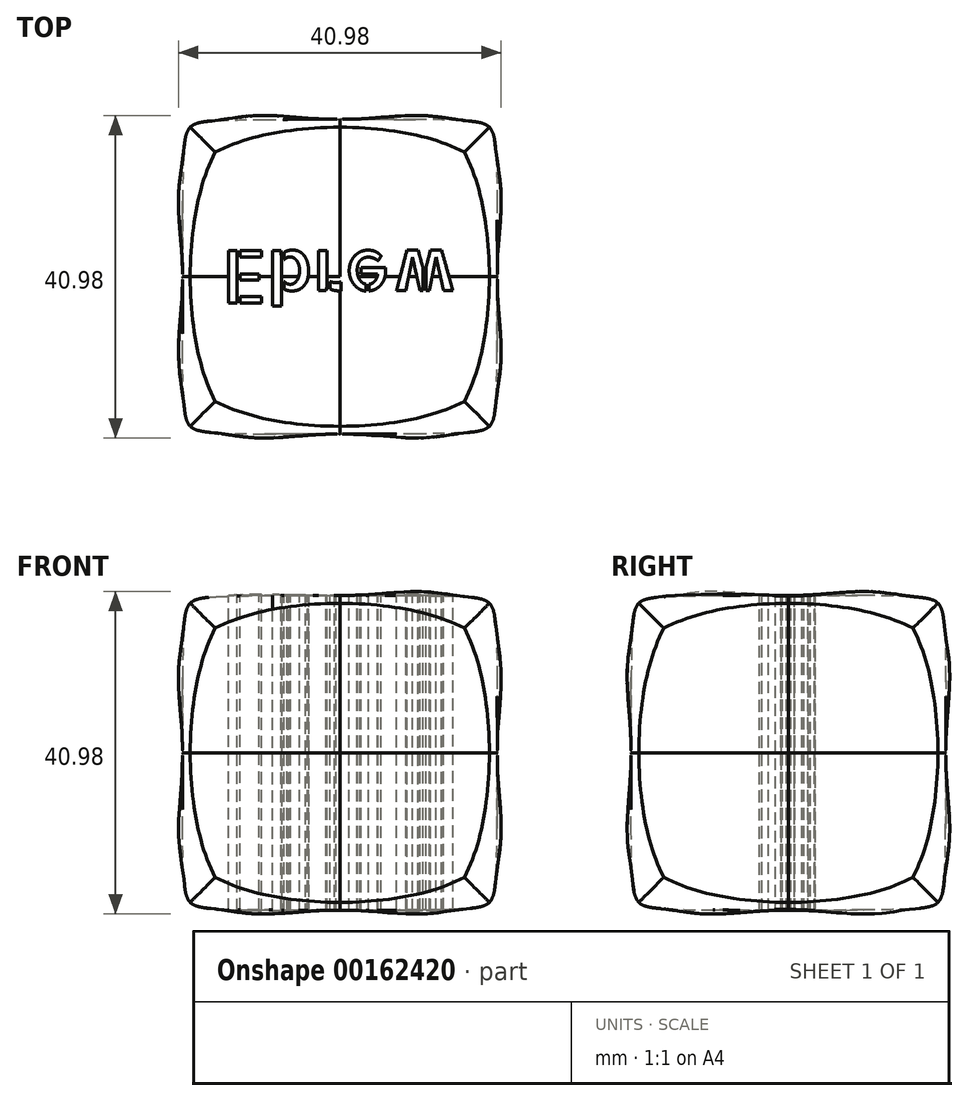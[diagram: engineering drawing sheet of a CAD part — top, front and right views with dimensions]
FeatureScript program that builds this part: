
annotation { "Feature Type Name" : "Feature", "Feature Type Description" : "" }
export const myFeature = defineFeature(function(context is Context, id is Id, definition is map)
    precondition{}
    {
        {
            var Q0;
            Q0=qCreatedBy(makeId("Top.planeOp"),FACE);
            var sketch = newSketch(context, id + "F0", { "sketchPlane" : qUnion([Q0])});
            skLineSegment(sketch, "E0.bottom", {"start": v(20, -20) * mm, "end": v(-20, -20) * mm});
            skLineSegment(sketch, "E0.top", {"start": v(20, 20) * mm, "end": v(-20, 20) * mm});
            skLineSegment(sketch, "E0.left", {"start": v(20, -20) * mm, "end": v(20, 20) * mm});
            skLineSegment(sketch, "E0.right", {"start": v(-20, -20) * mm, "end": v(-20, 20) * mm});
            skPoint(sketch, "E0.middle", {"position": v(0, 0) * mm});
            skSolve(sketch);
        }
        {
            var Q0;
            Q0 = qSketchRegion(id + "F0", true);
            extrude(context, id + "F1", {"entities" : qUnion([Q0]), "depth" : 40 * mm});
        }
        {
            var Q0;
            Q0=makeQuery(id+"F1.opExtrude","CAP_EDGE",EDGE,{"disambiguationData":[OSD([sQuery(id+"F0.wireOp",EDGE,"E0.right")])],"isStart":false});
            var Q1;
            Q1=makeQuery(id+"F1.opExtrude","SWEPT_FACE",FACE,{"disambiguationData":[OSD([sQuery(id+"F0.wireOp",EDGE,"E0.bottom")])]});
            var Q2;
            Q2=makeQuery(id+"F1.opExtrude","CAP_FACE",FACE,{"disambiguationData":[OSD([sQuery(id+"F0.wireOp",EDGE,"E0.bottom"),sQuery(id+"F0.wireOp",EDGE,"E0.top"),sQuery(id+"F0.wireOp",EDGE,"E0.left"),sQuery(id+"F0.wireOp",EDGE,"E0.right")])],"isStart":false});
            var Q3;
            Q3=makeQuery(id+"F1.opExtrude","SWEPT_FACE",FACE,{"disambiguationData":[OSD([sQuery(id+"F0.wireOp",EDGE,"E0.right")])]});
            var Q4;
            Q4=makeQuery(id+"F1.opExtrude","CAP_FACE",FACE,{"disambiguationData":[OSD([sQuery(id+"F0.wireOp",EDGE,"E0.bottom"),sQuery(id+"F0.wireOp",EDGE,"E0.top"),sQuery(id+"F0.wireOp",EDGE,"E0.left"),sQuery(id+"F0.wireOp",EDGE,"E0.right")])],"isStart":true});
            var Q5;
            Q5=makeQuery(id+"F1.opExtrude","SWEPT_FACE",FACE,{"disambiguationData":[OSD([sQuery(id+"F0.wireOp",EDGE,"E0.top")])]});
            fillet(context, id + "F2", {"entities" : qUnion([Q0, Q1, Q2, Q3, Q4, Q5]), "radius" : 20 * mm, "tangentPropagation" : true, "rho" : 0.9, "crossSection" : FilletCrossSection.CONIC, "allowEdgeOverflow" : false});
        }
        {
            var Q0;
            Q0=makeQuery(id+"F2.opFillet","BLEND_VERTEX",VERTEX,{"blendedFrom":[makeQuery(id+"F1.opExtrude","CAP_VERTEX",VERTEX,{"disambiguationData":[OSD([sQuery(id+"F0.wireOp",EDGE,"E0.top"),sQuery(id+"F0.wireOp",EDGE,"E0.left")])],"isStart":false})],"blendedInto":[]});
            var Q1;
            Q1=makeQuery(id+"F2.opFillet","BLEND_VERTEX",VERTEX,{"blendedFrom":[makeQuery(id+"F1.opExtrude","CAP_VERTEX",VERTEX,{"disambiguationData":[OSD([sQuery(id+"F0.wireOp",EDGE,"E0.top"),sQuery(id+"F0.wireOp",EDGE,"E0.right")])],"isStart":false})],"blendedInto":[]});
            var Q2;
            Q2=makeQuery(id+"F2.opFillet","BLEND_VERTEX",VERTEX,{"blendedFrom":[makeQuery(id+"F1.opExtrude","CAP_VERTEX",VERTEX,{"disambiguationData":[OSD([sQuery(id+"F0.wireOp",EDGE,"E0.bottom"),sQuery(id+"F0.wireOp",EDGE,"E0.left")])],"isStart":false})],"blendedInto":[]});
            cPlane(context, id + "F3", {"entities" : qUnion([Q0, Q1, Q2]), "cplaneType" : CPlaneType.THREE_POINT, "offset" : 25.4 * mm, "width" : 152.4 * mm, "height" : 152.4 * mm});
        }
        {
            var Q0;
            Q0=qCreatedBy(id+"F3.planeOp",FACE);
            cPlane(context, id + "F4", {"entities" : qUnion([Q0]), "cplaneType" : CPlaneType.OFFSET, "offset" : 5 * mm, "oppositeDirection" : true, "width" : 152.4 * mm, "height" : 152.4 * mm});
        }
        {
            var Q0;
            Q0=qCreatedBy(id+"F4.planeOp",FACE);
            var sketch = newSketch(context, id + "F5", { "sketchPlane" : qUnion([Q0])});
            skText(sketch, "E1", { "text": "Ebrew", "fontName": "AllertaStencil-Regular.ttf"});
            skLineSegment(sketch, "E2", {"start": v(-15, -3.34) * mm, "end": v(15, 3.34) * mm, "construction": true});
            skLineSegment(sketch, "E3", {"start": v(15, -3.34) * mm, "end": v(-15, 3.34) * mm, "construction": true});
            skPoint(sketch, "E4", {"position": v(0, 0) * mm});
            const initialGuessF5  = {"E1": [-0.015, -0.00334, 1, 0, 0.00668]};
            skSetInitialGuess(sketch, initialGuessF5);
            skSolve(sketch);
        }
        {
            var Q0;
            Q0 = qSketchRegion(id + "F5", true);
            extrude(context, id + "F6", {"entities" : qUnion([Q0]), "operationType" : NewBodyOperationType.REMOVE, "endBound" : BoundingType.THROUGH_ALL, "depth" : 25.4 * mm});
        }
    });
